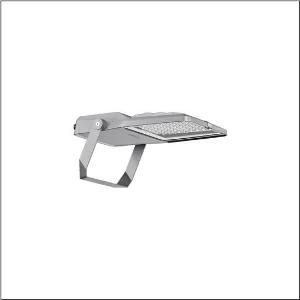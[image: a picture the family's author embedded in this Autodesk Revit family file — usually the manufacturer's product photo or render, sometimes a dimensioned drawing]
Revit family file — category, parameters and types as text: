
# Revit family: floodlight_fl_21_iq_mini___pl64_5xa7772d5e1a_506a
name_source: partatom
category: Lighting Fixtures
units: mm (PartAtom-declared; Revit-internal decimal feet)

## family parameters
Cut with Voids When Loaded = No
Host = Face
Light Source = No
Part Type = Normal
Room Calculation Point = No
Round Connector Dimension = Use Diameter
Shared = No

## types (1)
- --- (1 x LED, 16070 lm, 143 W, 4000K)
    Apparent Load = 143 VA
    CIE Flux Codes = 28 80 98 100 100
    Color Rendering = 80
    Color Temperature = 4000K
    Default Elevation = 1800 mm
    Description = Floodlight FL 21 iQ mini, floodlight, primary light control with lens, of PMMA, primary optical cover: protective disc, of toughened safety glass, transparent, light distribution: PL64, light emission: direct distribution, installation type: surface-mounted, lamps: LED, High Power LED, rated values: 16.070lm | 143W | 112,4lm/W (begin service life); end service life: 16.070lm | 151,6W; at 50% lumin. flux: 8.035lm | 60,6W | 132,6lm/W, colour temperature: 4000K, colour rendering: CRI > 80, light colour: 840, light setting 1 begin service life: 100% | 16.070lm | 143W | 112,4lm/W | 4.000K, light setting 1 end service life: 151,6W, further light settings possible, control: Street-Remote, Auto-Match, Temp-Guard, Night-Set, Smart-Wire, Desk-Remote (wireless, voltage-free reading and setting of iQ features in the workshop via application-optimized NFC function/RFID function), optimised constant luminous flux control (CLO 2.0), pre-setting: linear dimming characteristic, with terminal, 6-pole, mains connection: 220..240V, AC, 50/60Hz, luminaire housing, of diecast aluminium, powder-coated, SITECO metallic grey (DB 702S), corrosivity category C5 mid according to DIN EN ISO 12944suitable for swimming poolschlorine-resistant, sealing non-destructively replaceable, mounting bracket, of steel, galvanised, powder-coated, SITECO metallic grey (DB 702S), protection rating (complete): IP66, insulation class (complete): insulation class II (safety insulation), certification: CE, ENEC, VDE, protection symbol: D, impact resistance: IK08, permissible operating ambient temperature: -40..+40°C, permissible operating ambient temperature for outdoor applications: -40..+50°C, standard: DIN EN 12944, LABS conformity tested according to VDMA 24364:2018-05, packaging unit: 1 piece

Light Distribution: PL64
    Height = 70 mm
    Lamp = 1 x LED
    Lamp Light Flux = 16070 lm
    Lamp Power = 143 W
    Lamp count = 1
    Length = 485 mm
    Luminous efficacy = 112 lm/W
    Manufacturer = Siteco
    ModVariant = No
    Model = 5XA7772D5E1A
    Mounting Place = Pole
    Mounting Type = Pole annexe
    Number of Poles = 1
    OnlyDefault = Yes
    Power Factor = 1
    Product Name = Floodlight FL 21 iQ mini | PL64
    Product group = floodlight | pylon annexe
    ProductGroupID = 6201
    Protection Class = Protection class II
    Protection Degree = IP 66
    RLX_Detail_Level = 1
    RLX_Emergency_Light_Flux = 0 lm
    RLX_Emergency_Type = 0
    RLX_Emergency_Type_DB = No
    RlxData = <blob elided: 96629 chars, md5=95419efe>
    Socket = socket
    Standby Power = 0 W
    System Light Flux = 16070 lm
    System Power = 143 W
    Type Comments = factory setting: luminous flux: 100 % | dim-lin: 254 | 730 mA
    Type Image = l_1006845.jpg
    URL = http://relux.com
    VarID = @adj_166645
    Voltage = 0 V
    Weight = 0.00 kg
    Width = 337 mm

## geometry (parser evidence)
native form markers: Blend x4, Sweep x10
no freeform markers — native parametric forms only
